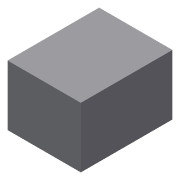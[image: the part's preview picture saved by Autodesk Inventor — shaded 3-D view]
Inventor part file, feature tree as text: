
AUTODESK INVENTOR PART (.ipt)
format: ipt  version: 2019 (Build 230136000, 136)  size: 72,704 bytes
history: native  units: mm
features: other x1, extrude x1, sketch x1
ambient origin geometry x8: Origin, YZ Plane, XZ Plane, XY Plane, X Axis, Y Axis, Z Axis, Center Point
bodies: Body1 (feature_tree)
feature tree (3):
  other  "솔리드1"
  extrude  "돌출1"  Depth=460.0mm
  sketch  "스케치1"
